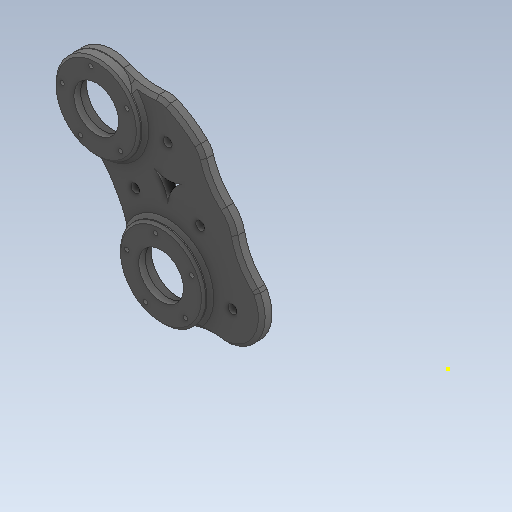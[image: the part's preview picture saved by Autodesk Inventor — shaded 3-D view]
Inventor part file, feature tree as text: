
AUTODESK INVENTOR PART (.ipt)
format: ipt  version: 2020 (Build 240168000, 168)  size: 350,720 bytes
history: native  units: mm
features: reference x8, sketch x5, other x4, extrude x4, chamfer x2
ambient origin geometry x8: Origin, YZ Plane, XZ Plane, XY Plane, X Axis, Y Axis, Z Axis, Center Point
bodies: Body1 (feature_tree)
feature tree (23):
  other  "Твердое тело1"
  other  "РабПлоскость1"
  extrude  "Выдавливание1"  Depth=47.8mm
  extrude  "Выдавливание2"  Depth=47.8mm
  chamfer  "Фаска1"  Distance=60.0mm
  chamfer  "Фаска2"  Distance=8.0mm
  sketch  "Эскиз3"
  extrude  "Выдавливание3"  Depth=8.0mm
  extrude  "Выдавливание4"  Depth=8.0mm
  sketch  "Эскиз1"
  reference  "Ссылка1"
  reference  "Ссылка2"
  reference  "Ссылка3"
  reference  "Ссылка4"
  reference  "Ссылка5"
  reference  "Ссылка6"
  sketch  "Эскиз2"
  reference  "Ссылка8"
  reference  "Ссылка9"
  sketch  "Эскиз4"
  sketch  "Эскиз5"
  other  "Сборка1"
  other  "block_new:1"
